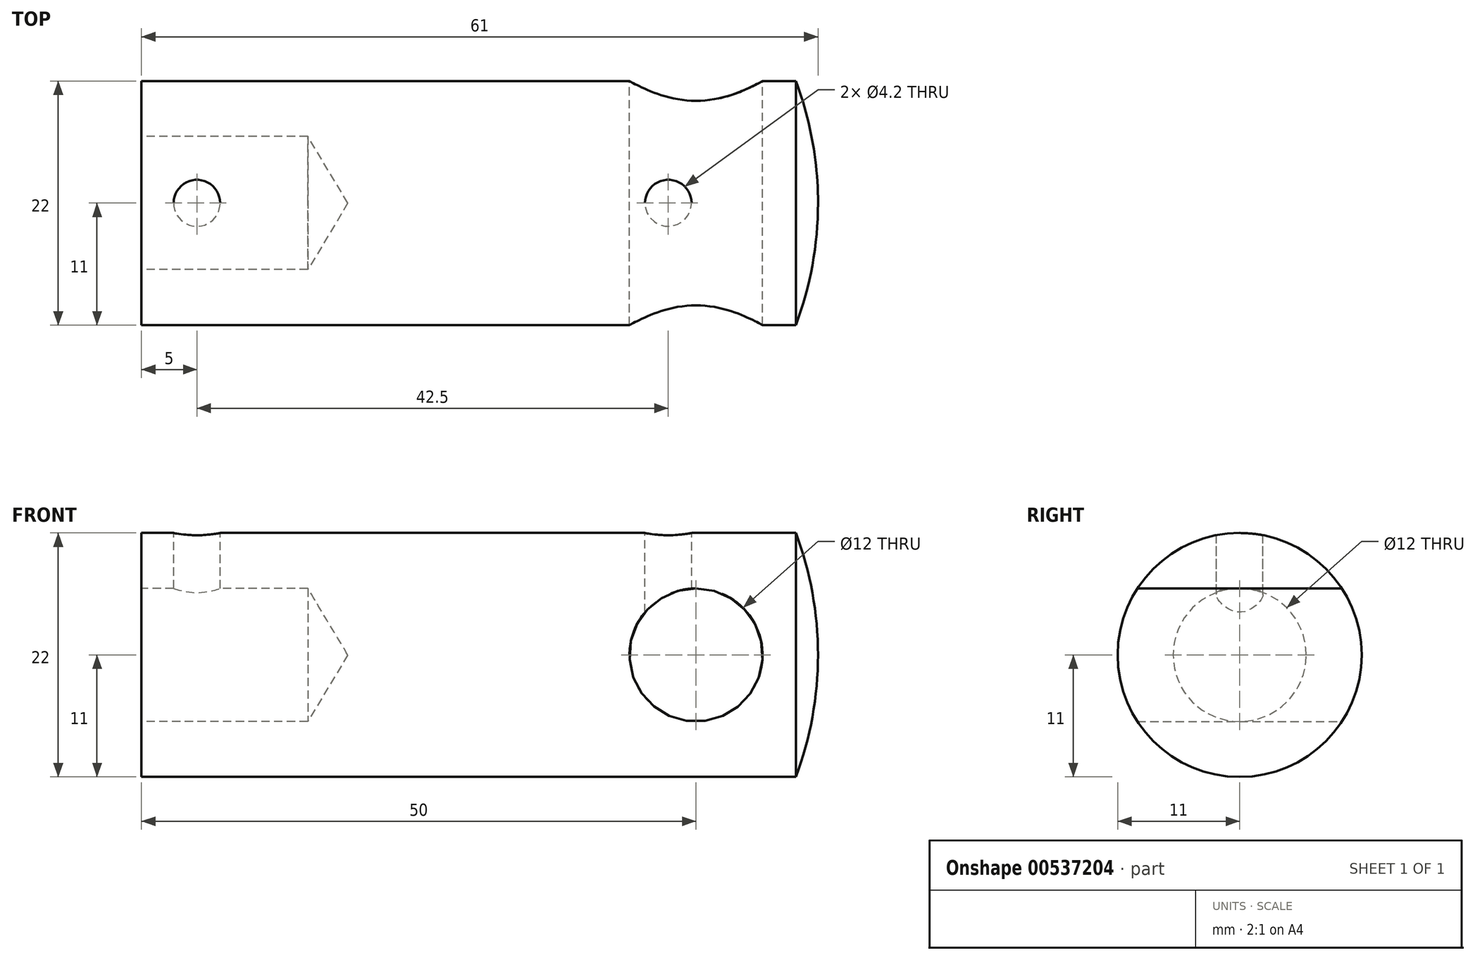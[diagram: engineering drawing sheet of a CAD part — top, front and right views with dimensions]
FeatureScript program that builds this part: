
annotation { "Feature Type Name" : "Feature", "Feature Type Description" : "" }
export const myFeature = defineFeature(function(context is Context, id is Id, definition is map)
    precondition{}
    {
        {
            var Q0;
            Q0=qCreatedBy(makeId("Top.planeOp"),FACE);
            var sketch = newSketch(context, id + "F0", { "sketchPlane" : qUnion([Q0])});
            skLineSegment(sketch, "E0", {"start": v(0, 0) * mm, "end": v(61, 0) * mm});
            skArc(sketch, "E1", {"start": v(61, 0) * mm, "mid": v(60.5, 5.6) * mm, "end": v(59, 11) * mm});
            skLineSegment(sketch, "E2", {"start": v(59, 11) * mm, "end": v(0, 11) * mm});
            skLineSegment(sketch, "E3", {"start": v(0, 11) * mm, "end": v(0, 0) * mm});
            skSolve(sketch);
        }
        {
            var Q0;
            Q0=makeQuery(id+"F0.imprint","IMPRINT",FACE,{"disambiguationData":[TD([[makeQuery(id+"F0.imprint","IMPRINT",EDGE,{"derivedFrom":sQuery(id+"F0.wireOp",EDGE,"E0")}),1.0]])]});
            var Q1;
            Q1=sQuery(id+"F0.wireOp",EDGE,"E0");
            revolve(context, id + "F1", {"entities" : qUnion([Q0]), "axis" : qUnion([Q1]), "revolveType" : RevolveType.FULL});
        }
        {
            var Q0;
            Q0=makeQuery(id+"F1.opRevolve","SWEPT_FACE",FACE,{"disambiguationData":[OSD([sQuery(id+"F0.wireOp",EDGE,"E3")])]});
            var sketch = newSketch(context, id + "F2", { "sketchPlane" : qUnion([Q0])});
            skPoint(sketch, "E4", {"position": v(0, 0) * mm});
            skSolve(sketch);
        }
        {
            var Q0;
            Q0=sQuery(id+"F2.wireOp",VERTEX,"E4");
            var Q1;
            Q1=makeQuery(id+"F1.opRevolve","SWEPT_BODY",BODY,{"disambiguationData":[OSD([sQuery(id+"F0.wireOp",EDGE,"E0"),sQuery(id+"F0.wireOp",EDGE,"E1"),sQuery(id+"F0.wireOp",EDGE,"E2"),sQuery(id+"F0.wireOp",EDGE,"E3")])]});
            hole(context, id + "F3", {"style" : HoleStyle.SIMPLE, "endStyle" : HoleEndStyle.BLIND, "holeDiameter" : 12 * mm, "holeDepth" : 15 * mm, "isTappedThrough" : true, "tappedDepth" : 12 * mm, "tapClearance" : 3, "locations" : qUnion([Q0]), "scope" : qUnion([Q1])});
        }
        {
            var Q0;
            Q0=qCreatedBy(makeId("Front.planeOp"),FACE);
            cPlane(context, id + "F4", {"entities" : qUnion([Q0]), "cplaneType" : CPlaneType.OFFSET, "offset" : 15 * mm, "oppositeDirection" : true, "width" : 150 * mm, "height" : 150 * mm});
        }
        {
            var Q0;
            Q0=qCreatedBy(id+"F4.planeOp",FACE);
            var sketch = newSketch(context, id + "F5", { "sketchPlane" : qUnion([Q0])});
            skPoint(sketch, "E5", {"position": v(50, 0) * mm});
            skSolve(sketch);
        }
        {
            var Q0;
            Q0=sQuery(id+"F5.wireOp",VERTEX,"E5");
            var Q1;
            Q1=makeQuery(id+"F1.opRevolve","SWEPT_BODY",BODY,{"disambiguationData":[OSD([sQuery(id+"F0.wireOp",EDGE,"E0"),sQuery(id+"F0.wireOp",EDGE,"E1"),sQuery(id+"F0.wireOp",EDGE,"E2"),sQuery(id+"F0.wireOp",EDGE,"E3")])]});
            hole(context, id + "F6", {"style" : HoleStyle.SIMPLE, "endStyle" : HoleEndStyle.THROUGH, "oppositeDirection" : true, "holeDiameter" : 12 * mm, "isTappedThrough" : true, "tappedDepth" : 12 * mm, "tapClearance" : 3, "locations" : qUnion([Q0]), "scope" : qUnion([Q1])});
        }
        {
            var Q0;
            Q0=qCreatedBy(makeId("Top.planeOp"),FACE);
            cPlane(context, id + "F7", {"entities" : qUnion([Q0]), "cplaneType" : CPlaneType.OFFSET, "offset" : 15 * mm, "width" : 150 * mm, "height" : 150 * mm});
        }
        {
            var Q0;
            Q0=qCreatedBy(id+"F7.planeOp",FACE);
            var sketch = newSketch(context, id + "F8", { "sketchPlane" : qUnion([Q0])});
            skPoint(sketch, "E6", {"position": v(5, 0) * mm});
            skPoint(sketch, "E7", {"position": v(47.5, 0) * mm});
            skSolve(sketch);
        }
        {
            var Q0;
            Q0=sQuery(id+"F8.wireOp",VERTEX,"E6");
            var Q1;
            Q1=sQuery(id+"F8.wireOp",VERTEX,"E7");
            var Q2;
            Q2=makeQuery(id+"F1.opRevolve","SWEPT_BODY",BODY,{"disambiguationData":[OSD([sQuery(id+"F0.wireOp",EDGE,"E0"),sQuery(id+"F0.wireOp",EDGE,"E1"),sQuery(id+"F0.wireOp",EDGE,"E2"),sQuery(id+"F0.wireOp",EDGE,"E3")])]});
            hole(context, id + "F9", {"style" : HoleStyle.SIMPLE, "endStyle" : HoleEndStyle.BLIND, "holeDiameter" : 4.2 * mm, "holeDepth" : 12 * mm, "isTappedThrough" : true, "tappedDepth" : 12 * mm, "tapClearance" : 3, "locations" : qUnion([Q0, Q1]), "scope" : qUnion([Q2])});
        }
    });
